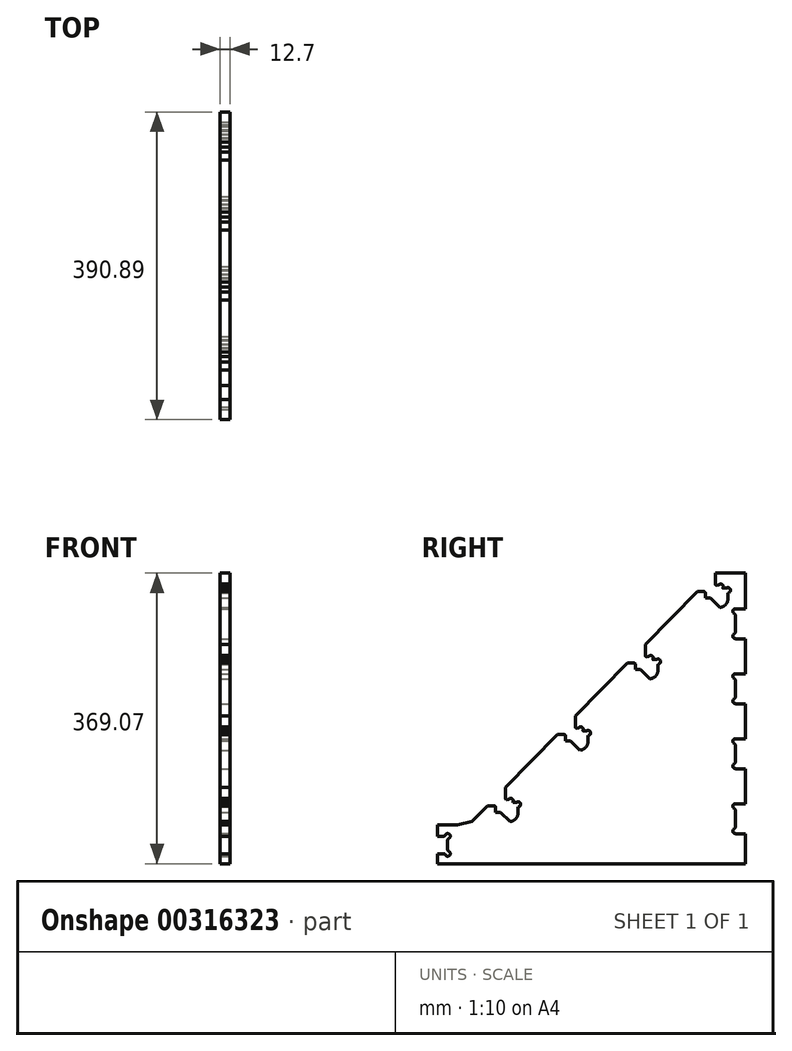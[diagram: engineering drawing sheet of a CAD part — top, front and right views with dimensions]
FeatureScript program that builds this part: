
annotation { "Feature Type Name" : "Feature", "Feature Type Description" : "" }
export const myFeature = defineFeature(function(context is Context, id is Id, definition is map)
    precondition{}
    {
        {
            var Q0;
            Q0=qCreatedBy(makeId("Right.planeOp"),FACE);
            var sketch = newSketch(context, id + "F0", { "sketchPlane" : qUnion([Q0])});
            skLineSegment(sketch, "E0", {"start": v(304.8, 304.8) * mm, "end": v(266.7, 304.85) * mm});
            skLineSegment(sketch, "E1.5.0.0", {"start": v(-60.7, -29.3) * mm, "end": v(-60.7, -64.22) * mm});
            skLineSegment(sketch, "E2", {"start": v(-60.7, -64.22) * mm, "end": v(304.8, -64.22) * mm});
            skLineSegment(sketch, "E3", {"start": v(304.8, 304.8) * mm, "end": v(304.8, -64.22) * mm});
            skLineSegment(sketch, "E4", {"start": v(-42.51, -10.74) * mm, "end": v(266.7, 304.85) * mm});
            skLineSegment(sketch, "E5", {"start": v(-60.7, -29.3) * mm, "end": v(-60.7, -19.79) * mm});
            skLineSegment(sketch, "E6", {"start": v(-60.7, -19.79) * mm, "end": v(-60.7, -14.97) * mm});
            skLineSegment(sketch, "E7", {"start": v(-60.7, -14.97) * mm, "end": v(-42.51, -10.74) * mm});
            skLineSegment(sketch, "E8", {"start": v(-60.7, -14.97) * mm, "end": v(-86.1, -14.97) * mm});
            skLineSegment(sketch, "E9", {"start": v(-86.1, -14.97) * mm, "end": v(-86.1, -64.22) * mm});
            skLineSegment(sketch, "E10", {"start": v(-60.7, -64.22) * mm, "end": v(-86.1, -64.22) * mm});
            skSolve(sketch);
        }
        {
            var Q0;
            Q0 = qSketchRegion(id + "F0", true);
            extrude(context, id + "F1", {"entities" : qUnion([Q0]), "depth" : 12.7 * mm});
        }
        {
            var Q0;
            Q0 = qSketchRegion(id + "F0", true);
            extrude(context, id + "F2", {"entities" : qUnion([Q0]), "operationType" : NewBodyOperationType.ADD, "depth" : 12.7 * mm});
        }
        {
            var Q0;
            Q0=makeQuery(id+"F1.opExtrude","CAP_FACE",FACE,{"disambiguationData":[OSD([sQuery(id+"F0.wireOp",EDGE,"E0"),sQuery(id+"F0.wireOp",EDGE,"E1.5.0.0"),sQuery(id+"F0.wireOp",EDGE,"E2"),sQuery(id+"F0.wireOp",EDGE,"E3"),sQuery(id+"F0.wireOp",EDGE,"01d1fe62-4fe1-469e-83bf-c5be6320b151.1.0.1"),sQuery(id+"F0.wireOp",EDGE,"01d1fe62-4fe1-469e-83bf-c5be6320b151.1.0.6"),sQuery(id+"F0.wireOp",EDGE,"01d1fe62-4fe1-469e-83bf-c5be6320b151.1.0.10"),sQuery(id+"F0.wireOp",EDGE,"01d1fe62-4fe1-469e-83bf-c5be6320b151.1.0.11"),sQuery(id+"F0.wireOp",EDGE,"01d1fe62-4fe1-469e-83bf-c5be6320b151.1.0.12"),sQuery(id+"F0.wireOp",EDGE,"01d1fe62-4fe1-469e-83bf-c5be6320b151.1.0.13"),sQuery(id+"F0.wireOp",EDGE,"01d1fe62-4fe1-469e-83bf-c5be6320b151.1.0.14"),sQuery(id+"F0.wireOp",EDGE,"01d1fe62-4fe1-469e-83bf-c5be6320b151.1.0.15"),sQuery(id+"F0.wireOp",EDGE,"01d1fe62-4fe1-469e-83bf-c5be6320b151.1.0.16"),sQuery(id+"F0.wireOp",EDGE,"01d1fe62-4fe1-469e-83bf-c5be6320b151.1.0.17"),sQuery(id+"F0.wireOp",EDGE,"01d1fe62-4fe1-469e-83bf-c5be6320b151.1.0.18"),sQuery(id+"F0.wireOp",EDGE,"01d1fe62-4fe1-469e-83bf-c5be6320b151.1.0.19"),sQuery(id+"F0.wireOp",EDGE,"46222585-26b9-4988-8b94-4dfa3d22ff35"),sQuery(id+"F0.wireOp",EDGE,"b57ab49b-1e31-4e1b-bc73-54784041036c"),sQuery(id+"F0.wireOp",EDGE,"5dba5122-0782-4218-805a-b523ed69a662"),sQuery(id+"F0.wireOp",EDGE,"LXE0opSN-cuTV-U9b0-HqBj-6hOjDb2a0Kfw"),sQuery(id+"F0.wireOp",EDGE,"E4")])],"isStart":false});
            var sketch = newSketch(context, id + "F3", { "sketchPlane" : qUnion([Q0])});
            skArc(sketch, "E11.1.0.1", {"start": v(272.19, 261.27) * mm, "mid": v(279.87, 265.04) * mm, "end": v(282.61, 273.14) * mm});
            skPoint(sketch, "E11.1.0.9", {"position": v(266.74, 285.89) * mm});
            skLineSegment(sketch, "E11.1.0.10", {"start": v(266.74, 304.93) * mm, "end": v(266.74, 291.08) * mm});
            skLineSegment(sketch, "E11.1.0.11", {"start": v(260.44, 273.14) * mm, "end": v(272.19, 261.27) * mm});
            skArc(sketch, "E11.1.0.12", {"start": v(266.74, 291.08) * mm, "mid": v(266.95, 289.96) * mm, "end": v(267.4, 288.92) * mm});
            skLineSegment(sketch, "E11.1.0.14", {"start": v(260.44, 273.14) * mm, "end": v(254.04, 273.14) * mm});
            skLineSegment(sketch, "E12", {"start": v(267.4, 288.92) * mm, "end": v(270.65, 289.62) * mm});
            skLineSegment(sketch, "E13", {"start": v(266.74, 304.93) * mm, "end": v(243.65, 281.33) * mm});
            skLineSegment(sketch, "E14", {"start": v(276.24, 285.84) * mm, "end": v(280.77, 285.84) * mm});
            skLineSegment(sketch, "E15", {"start": v(254.04, 273.14) * mm, "end": v(254.04, 279.3) * mm});
            skLineSegment(sketch, "E16", {"start": v(252, 281.33) * mm, "end": v(243.65, 281.33) * mm});
            skPoint(sketch, "E17.visualSharp", {"position": v(254.04, 281.33) * mm});
            skArc(sketch, "E17.filletArc", {"start": v(254.04, 279.3) * mm, "mid": v(253.44, 280.73) * mm, "end": v(252, 281.33) * mm});
            skArc(sketch, "E18", {"start": v(282.61, 279.8) * mm, "mid": v(285.77, 284.06) * mm, "end": v(280.77, 285.84) * mm});
            skLineSegment(sketch, "E19.trimOffspring", {"start": v(282.61, 279.8) * mm, "end": v(282.61, 273.14) * mm});
            skPoint(sketch, "E20.orphan", {"position": v(282.62, 285.84) * mm});
            skArc(sketch, "E21", {"start": v(276.17, 286.02) * mm, "mid": v(275.1, 290.41) * mm, "end": v(270.65, 289.62) * mm});
            skPoint(sketch, "E22.orphan", {"position": v(274.56, 290.46) * mm});
            skPoint(sketch, "E23.orphan", {"position": v(275.55, 285.84) * mm});
            skArc(sketch, "E24", {"start": v(276.17, 286.02) * mm, "mid": v(276.17, 285.91) * mm, "end": v(276.24, 285.84) * mm});
            skLineSegment(sketch, "E25.1.0.0", {"start": v(177.84, 214.22) * mm, "end": v(177.84, 200.37) * mm});
            skLineSegment(sketch, "E25.1.0.1", {"start": v(171.55, 182.43) * mm, "end": v(183.3, 170.57) * mm});
            skArc(sketch, "E25.1.0.2", {"start": v(183.3, 170.57) * mm, "mid": v(190.97, 174.34) * mm, "end": v(193.72, 182.43) * mm});
            skPoint(sketch, "E25.1.0.3", {"position": v(185.66, 199.76) * mm});
            skLineSegment(sketch, "E25.1.0.4", {"start": v(177.84, 214.22) * mm, "end": v(154.75, 190.62) * mm});
            skPoint(sketch, "E25.1.0.5", {"position": v(193.72, 195.13) * mm});
            skPoint(sketch, "E25.1.0.6", {"position": v(165.14, 190.62) * mm});
            skPoint(sketch, "E25.1.0.7", {"position": v(186.66, 195.13) * mm});
            skPoint(sketch, "E25.1.0.8", {"position": v(177.85, 195.19) * mm});
            skLineSegment(sketch, "E25.1.0.9", {"start": v(193.72, 189.1) * mm, "end": v(193.72, 182.43) * mm});
            skLineSegment(sketch, "E25.1.0.10", {"start": v(171.55, 182.43) * mm, "end": v(165.14, 182.43) * mm});
            skLineSegment(sketch, "E25.1.0.11", {"start": v(165.14, 182.43) * mm, "end": v(165.14, 188.6) * mm});
            skLineSegment(sketch, "E25.1.0.12", {"start": v(163.11, 190.62) * mm, "end": v(154.75, 190.62) * mm});
            skArc(sketch, "E25.1.0.13", {"start": v(187.28, 195.32) * mm, "mid": v(186.21, 199.7) * mm, "end": v(181.76, 198.92) * mm});
            skArc(sketch, "E25.1.0.14", {"start": v(177.84, 200.37) * mm, "mid": v(178.06, 199.26) * mm, "end": v(178.5, 198.22) * mm});
            skArc(sketch, "E25.1.0.15", {"start": v(193.72, 189.1) * mm, "mid": v(196.88, 193.36) * mm, "end": v(191.88, 195.13) * mm});
            skLineSegment(sketch, "E25.1.0.16", {"start": v(178.5, 198.22) * mm, "end": v(181.76, 198.92) * mm});
            skArc(sketch, "E25.1.0.17", {"start": v(165.14, 188.6) * mm, "mid": v(164.55, 190.03) * mm, "end": v(163.11, 190.62) * mm});
            skLineSegment(sketch, "E25.1.0.18", {"start": v(187.35, 195.13) * mm, "end": v(191.88, 195.13) * mm});
            skArc(sketch, "E25.1.0.19", {"start": v(187.28, 195.32) * mm, "mid": v(187.27, 195.21) * mm, "end": v(187.35, 195.13) * mm});
            skLineSegment(sketch, "E25.2.0.0", {"start": v(88.95, 123.52) * mm, "end": v(88.95, 109.67) * mm});
            skLineSegment(sketch, "E25.2.0.1", {"start": v(82.65, 91.73) * mm, "end": v(94.4, 79.87) * mm});
            skArc(sketch, "E25.2.0.2", {"start": v(94.4, 79.87) * mm, "mid": v(102.08, 83.63) * mm, "end": v(104.82, 91.73) * mm});
            skPoint(sketch, "E25.2.0.3", {"position": v(96.77, 109.06) * mm});
            skLineSegment(sketch, "E25.2.0.4", {"start": v(88.95, 123.52) * mm, "end": v(65.86, 99.92) * mm});
            skPoint(sketch, "E25.2.0.5", {"position": v(104.83, 104.43) * mm});
            skPoint(sketch, "E25.2.0.6", {"position": v(76.25, 99.92) * mm});
            skPoint(sketch, "E25.2.0.7", {"position": v(97.77, 104.43) * mm});
            skPoint(sketch, "E25.2.0.8", {"position": v(88.95, 104.48) * mm});
            skLineSegment(sketch, "E25.2.0.9", {"start": v(104.83, 98.4) * mm, "end": v(104.82, 91.73) * mm});
            skLineSegment(sketch, "E25.2.0.10", {"start": v(82.65, 91.73) * mm, "end": v(76.25, 91.73) * mm});
            skLineSegment(sketch, "E25.2.0.11", {"start": v(76.25, 91.73) * mm, "end": v(76.25, 97.9) * mm});
            skLineSegment(sketch, "E25.2.0.12", {"start": v(74.22, 99.92) * mm, "end": v(65.86, 99.92) * mm});
            skArc(sketch, "E25.2.0.13", {"start": v(98.39, 104.61) * mm, "mid": v(97.32, 109) * mm, "end": v(92.87, 108.22) * mm});
            skArc(sketch, "E25.2.0.14", {"start": v(88.95, 109.67) * mm, "mid": v(89.16, 108.56) * mm, "end": v(89.61, 107.52) * mm});
            skArc(sketch, "E25.2.0.15", {"start": v(104.83, 98.4) * mm, "mid": v(107.99, 102.66) * mm, "end": v(102.98, 104.43) * mm});
            skLineSegment(sketch, "E25.2.0.16", {"start": v(89.61, 107.52) * mm, "end": v(92.87, 108.22) * mm});
            skArc(sketch, "E25.2.0.17", {"start": v(76.25, 97.9) * mm, "mid": v(75.65, 99.33) * mm, "end": v(74.22, 99.92) * mm});
            skLineSegment(sketch, "E25.2.0.18", {"start": v(98.45, 104.43) * mm, "end": v(102.98, 104.43) * mm});
            skArc(sketch, "E25.2.0.19", {"start": v(98.39, 104.61) * mm, "mid": v(98.38, 104.5) * mm, "end": v(98.45, 104.43) * mm});
            skLineSegment(sketch, "E25.3.0.0", {"start": v(0.05, 32.82) * mm, "end": v(0.05, 18.97) * mm});
            skLineSegment(sketch, "E25.3.0.1", {"start": v(-6.24, 1.03) * mm, "end": v(5.5, -10.83) * mm});
            skArc(sketch, "E25.3.0.2", {"start": v(5.5, -10.83) * mm, "mid": v(13.18, -7.07) * mm, "end": v(15.93, 1.03) * mm});
            skPoint(sketch, "E25.3.0.3", {"position": v(7.88, 18.36) * mm});
            skLineSegment(sketch, "E25.3.0.4", {"start": v(0.05, 32.82) * mm, "end": v(-23.03, 9.22) * mm});
            skPoint(sketch, "E25.3.0.5", {"position": v(15.93, 13.73) * mm});
            skPoint(sketch, "E25.3.0.6", {"position": v(-12.65, 9.22) * mm});
            skPoint(sketch, "E25.3.0.7", {"position": v(8.87, 13.73) * mm});
            skPoint(sketch, "E25.3.0.8", {"position": v(0.06, 13.78) * mm});
            skLineSegment(sketch, "E25.3.0.9", {"start": v(15.93, 7.69) * mm, "end": v(15.93, 1.03) * mm});
            skLineSegment(sketch, "E25.3.0.10", {"start": v(-6.24, 1.03) * mm, "end": v(-12.65, 1.03) * mm});
            skLineSegment(sketch, "E25.3.0.11", {"start": v(-12.65, 1.03) * mm, "end": v(-12.65, 7.19) * mm});
            skLineSegment(sketch, "E25.3.0.12", {"start": v(-14.68, 9.22) * mm, "end": v(-23.03, 9.22) * mm});
            skArc(sketch, "E25.3.0.13", {"start": v(9.5, 13.91) * mm, "mid": v(8.42, 18.3) * mm, "end": v(3.97, 17.52) * mm});
            skArc(sketch, "E25.3.0.14", {"start": v(0.05, 18.97) * mm, "mid": v(0.27, 17.86) * mm, "end": v(0.72, 16.81) * mm});
            skArc(sketch, "E25.3.0.15", {"start": v(15.93, 7.69) * mm, "mid": v(19.1, 11.96) * mm, "end": v(14.09, 13.73) * mm});
            skLineSegment(sketch, "E25.3.0.16", {"start": v(0.72, 16.81) * mm, "end": v(3.97, 17.52) * mm});
            skArc(sketch, "E25.3.0.17", {"start": v(-12.65, 7.19) * mm, "mid": v(-13.24, 8.63) * mm, "end": v(-14.68, 9.22) * mm});
            skLineSegment(sketch, "E25.3.0.18", {"start": v(9.56, 13.73) * mm, "end": v(14.09, 13.73) * mm});
            skArc(sketch, "E25.3.0.19", {"start": v(9.5, 13.91) * mm, "mid": v(9.48, 13.8) * mm, "end": v(9.56, 13.73) * mm});
            skLineSegment(sketch, "E25.direction1", {"start": v(243.65, 281.33) * mm, "end": v(154.75, 190.62) * mm, "construction": true});
            skSolve(sketch);
        }
        {
            var Q0;
            Q0 = qSketchRegion(id + "F3", true);
            extrude(context, id + "F4", {"entities" : qUnion([Q0]), "operationType" : NewBodyOperationType.REMOVE, "oppositeDirection" : true, "depth" : 25.4 * mm});
        }
        {
            var Q0;
            Q0=makeQuery(id+"F1.opExtrude","CAP_FACE",FACE,{"disambiguationData":[OSD([sQuery(id+"F0.wireOp",EDGE,"E0"),sQuery(id+"F0.wireOp",EDGE,"E1.5.0.0"),sQuery(id+"F0.wireOp",EDGE,"E2"),sQuery(id+"F0.wireOp",EDGE,"E3"),sQuery(id+"F0.wireOp",EDGE,"E4")])],"isStart":false});
            var sketch = newSketch(context, id + "F5", { "sketchPlane" : qUnion([Q0])});
            skLineSegment(sketch, "E26.bottom", {"start": v(304.8, -26.12) * mm, "end": v(292.1, -26.12) * mm});
            skLineSegment(sketch, "E26.top", {"start": v(304.8, 11.98) * mm, "end": v(292.1, 11.98) * mm});
            skLineSegment(sketch, "E26.left", {"start": v(304.8, -26.12) * mm, "end": v(304.8, 11.98) * mm});
            skArc(sketch, "E27", {"start": v(292.1, 11.98) * mm, "mid": v(288.9, 9.51) * mm, "end": v(290.48, 5.8) * mm});
            skArc(sketch, "E28", {"start": v(290.48, -19.94) * mm, "mid": v(288.9, -23.66) * mm, "end": v(292.1, -26.12) * mm});
            skLineSegment(sketch, "E29.trimOffspring", {"start": v(292.1, -17.17) * mm, "end": v(292.1, 3.03) * mm});
            skPoint(sketch, "E30.visualSharp", {"position": v(292.1, 5.37) * mm});
            skArc(sketch, "E30.filletArc", {"start": v(292.1, 3.03) * mm, "mid": v(291.67, 4.63) * mm, "end": v(290.48, 5.8) * mm});
            skPoint(sketch, "E31.visualSharp", {"position": v(292.1, -19.52) * mm});
            skArc(sketch, "E31.filletArc", {"start": v(290.48, -19.94) * mm, "mid": v(291.67, -18.78) * mm, "end": v(292.1, -17.17) * mm});
            skPoint(sketch, "E32.0.1.0", {"position": v(292.1, 87.92) * mm});
            skArc(sketch, "E32.0.1.1", {"start": v(292.1, 94.53) * mm, "mid": v(288.9, 92.06) * mm, "end": v(290.48, 88.35) * mm});
            skLineSegment(sketch, "E32.0.1.2", {"start": v(304.8, 56.43) * mm, "end": v(292.1, 56.43) * mm});
            skLineSegment(sketch, "E32.0.1.3", {"start": v(292.1, 65.38) * mm, "end": v(292.1, 85.58) * mm});
            skArc(sketch, "E32.0.1.4", {"start": v(290.48, 62.6) * mm, "mid": v(288.9, 58.9) * mm, "end": v(292.1, 56.43) * mm});
            skPoint(sketch, "E32.0.1.5", {"position": v(292.1, 63.03) * mm});
            skLineSegment(sketch, "E32.0.1.6", {"start": v(304.8, 56.43) * mm, "end": v(304.8, 94.53) * mm});
            skLineSegment(sketch, "E32.0.1.7", {"start": v(304.8, 94.53) * mm, "end": v(292.1, 94.53) * mm});
            skArc(sketch, "E32.0.1.8", {"start": v(292.1, 85.58) * mm, "mid": v(291.67, 87.18) * mm, "end": v(290.48, 88.35) * mm});
            skArc(sketch, "E32.0.1.9", {"start": v(290.48, 62.6) * mm, "mid": v(291.67, 63.77) * mm, "end": v(292.1, 65.38) * mm});
            skPoint(sketch, "E32.0.2.0", {"position": v(292.1, 170.47) * mm});
            skArc(sketch, "E32.0.2.1", {"start": v(292.1, 177.08) * mm, "mid": v(288.9, 174.61) * mm, "end": v(290.48, 170.9) * mm});
            skLineSegment(sketch, "E32.0.2.2", {"start": v(304.8, 138.98) * mm, "end": v(292.1, 138.98) * mm});
            skLineSegment(sketch, "E32.0.2.3", {"start": v(292.1, 147.93) * mm, "end": v(292.1, 168.13) * mm});
            skArc(sketch, "E32.0.2.4", {"start": v(290.48, 145.16) * mm, "mid": v(288.9, 141.44) * mm, "end": v(292.1, 138.98) * mm});
            skPoint(sketch, "E32.0.2.5", {"position": v(292.1, 145.58) * mm});
            skLineSegment(sketch, "E32.0.2.6", {"start": v(304.8, 138.98) * mm, "end": v(304.8, 177.08) * mm});
            skLineSegment(sketch, "E32.0.2.7", {"start": v(304.8, 177.08) * mm, "end": v(292.1, 177.08) * mm});
            skArc(sketch, "E32.0.2.8", {"start": v(292.1, 168.13) * mm, "mid": v(291.67, 169.73) * mm, "end": v(290.48, 170.9) * mm});
            skArc(sketch, "E32.0.2.9", {"start": v(290.48, 145.16) * mm, "mid": v(291.67, 146.32) * mm, "end": v(292.1, 147.93) * mm});
            skPoint(sketch, "E32.0.3.0", {"position": v(292.1, 253.02) * mm});
            skArc(sketch, "E32.0.3.1", {"start": v(292.1, 259.63) * mm, "mid": v(288.9, 257.16) * mm, "end": v(290.48, 253.45) * mm});
            skLineSegment(sketch, "E32.0.3.2", {"start": v(304.8, 221.53) * mm, "end": v(292.1, 221.53) * mm});
            skLineSegment(sketch, "E32.0.3.3", {"start": v(292.1, 230.48) * mm, "end": v(292.1, 250.68) * mm});
            skArc(sketch, "E32.0.3.4", {"start": v(290.48, 227.7) * mm, "mid": v(288.9, 224) * mm, "end": v(292.1, 221.53) * mm});
            skPoint(sketch, "E32.0.3.5", {"position": v(292.1, 228.13) * mm});
            skLineSegment(sketch, "E32.0.3.6", {"start": v(304.8, 221.53) * mm, "end": v(304.8, 259.63) * mm});
            skLineSegment(sketch, "E32.0.3.7", {"start": v(304.8, 259.63) * mm, "end": v(292.1, 259.63) * mm});
            skArc(sketch, "E32.0.3.8", {"start": v(292.1, 250.68) * mm, "mid": v(291.67, 252.28) * mm, "end": v(290.48, 253.45) * mm});
            skArc(sketch, "E32.0.3.9", {"start": v(290.48, 227.7) * mm, "mid": v(291.67, 228.87) * mm, "end": v(292.1, 230.48) * mm});
            skLineSegment(sketch, "E32.direction1", {"start": v(292.1, -26.12) * mm, "end": v(317.5, -26.12) * mm, "construction": true});
            skLineSegment(sketch, "E32.direction2", {"start": v(292.1, -26.12) * mm, "end": v(292.1, 56.43) * mm, "construction": true});
            skSolve(sketch);
        }
        {
            var Q0;
            Q0 = qSketchRegion(id + "F5", true);
            extrude(context, id + "F6", {"entities" : qUnion([Q0]), "operationType" : NewBodyOperationType.REMOVE, "oppositeDirection" : true, "depth" : 25.4 * mm});
        }
        {
            var Q0;
            Q0=makeQuery(id+"F1.opExtrude","CAP_FACE",FACE,{"disambiguationData":[OSD([sQuery(id+"F0.wireOp",EDGE,"E0"),sQuery(id+"F0.wireOp",EDGE,"E1.5.0.0"),sQuery(id+"F0.wireOp",EDGE,"E2"),sQuery(id+"F0.wireOp",EDGE,"E3"),sQuery(id+"F0.wireOp",EDGE,"E4"),sQuery(id+"F0.wireOp",EDGE,"E5"),sQuery(id+"F0.wireOp",EDGE,"E6"),sQuery(id+"F0.wireOp",EDGE,"E7")])],"isStart":false});
            var sketch = newSketch(context, id + "F7", { "sketchPlane" : qUnion([Q0])});
            skLineSegment(sketch, "E33.bottom", {"start": v(-86.1, -29.3) * mm, "end": v(-78.32, -29.3) * mm});
            skLineSegment(sketch, "E33.top", {"start": v(-86.1, -51.52) * mm, "end": v(-78.32, -51.52) * mm});
            skLineSegment(sketch, "E33.left", {"start": v(-86.1, -29.3) * mm, "end": v(-86.1, -51.52) * mm});
            skLineSegment(sketch, "E33.right", {"start": v(-73.4, -34.23) * mm, "end": v(-73.4, -46.59) * mm});
            skArc(sketch, "E34", {"start": v(-72.13, -32.35) * mm, "mid": v(-71.06, -26.96) * mm, "end": v(-76.44, -28.04) * mm});
            skArc(sketch, "E35", {"start": v(-76.44, -52.78) * mm, "mid": v(-71.06, -53.86) * mm, "end": v(-72.13, -48.47) * mm});
            skPoint(sketch, "E36.visualSharp", {"position": v(-76.7, -51.52) * mm});
            skArc(sketch, "E36.filletArc", {"start": v(-76.44, -52.78) * mm, "mid": v(-77.2, -51.86) * mm, "end": v(-78.32, -51.52) * mm});
            skPoint(sketch, "E37.visualSharp", {"position": v(-73.4, -48.22) * mm});
            skArc(sketch, "E37.filletArc", {"start": v(-73.4, -46.59) * mm, "mid": v(-73.05, -47.72) * mm, "end": v(-72.13, -48.47) * mm});
            skPoint(sketch, "E38.visualSharp", {"position": v(-73.4, -32.6) * mm});
            skArc(sketch, "E38.filletArc", {"start": v(-72.13, -32.35) * mm, "mid": v(-73.05, -33.1) * mm, "end": v(-73.4, -34.23) * mm});
            skPoint(sketch, "E39.visualSharp", {"position": v(-76.7, -29.3) * mm});
            skArc(sketch, "E39.filletArc", {"start": v(-78.32, -29.3) * mm, "mid": v(-77.2, -28.95) * mm, "end": v(-76.44, -28.04) * mm});
            skSolve(sketch);
        }
        {
            var Q0;
            Q0 = qSketchRegion(id + "F7", true);
            extrude(context, id + "F8", {"entities" : qUnion([Q0]), "operationType" : NewBodyOperationType.REMOVE, "oppositeDirection" : true, "depth" : 25.4 * mm});
        }
    });
